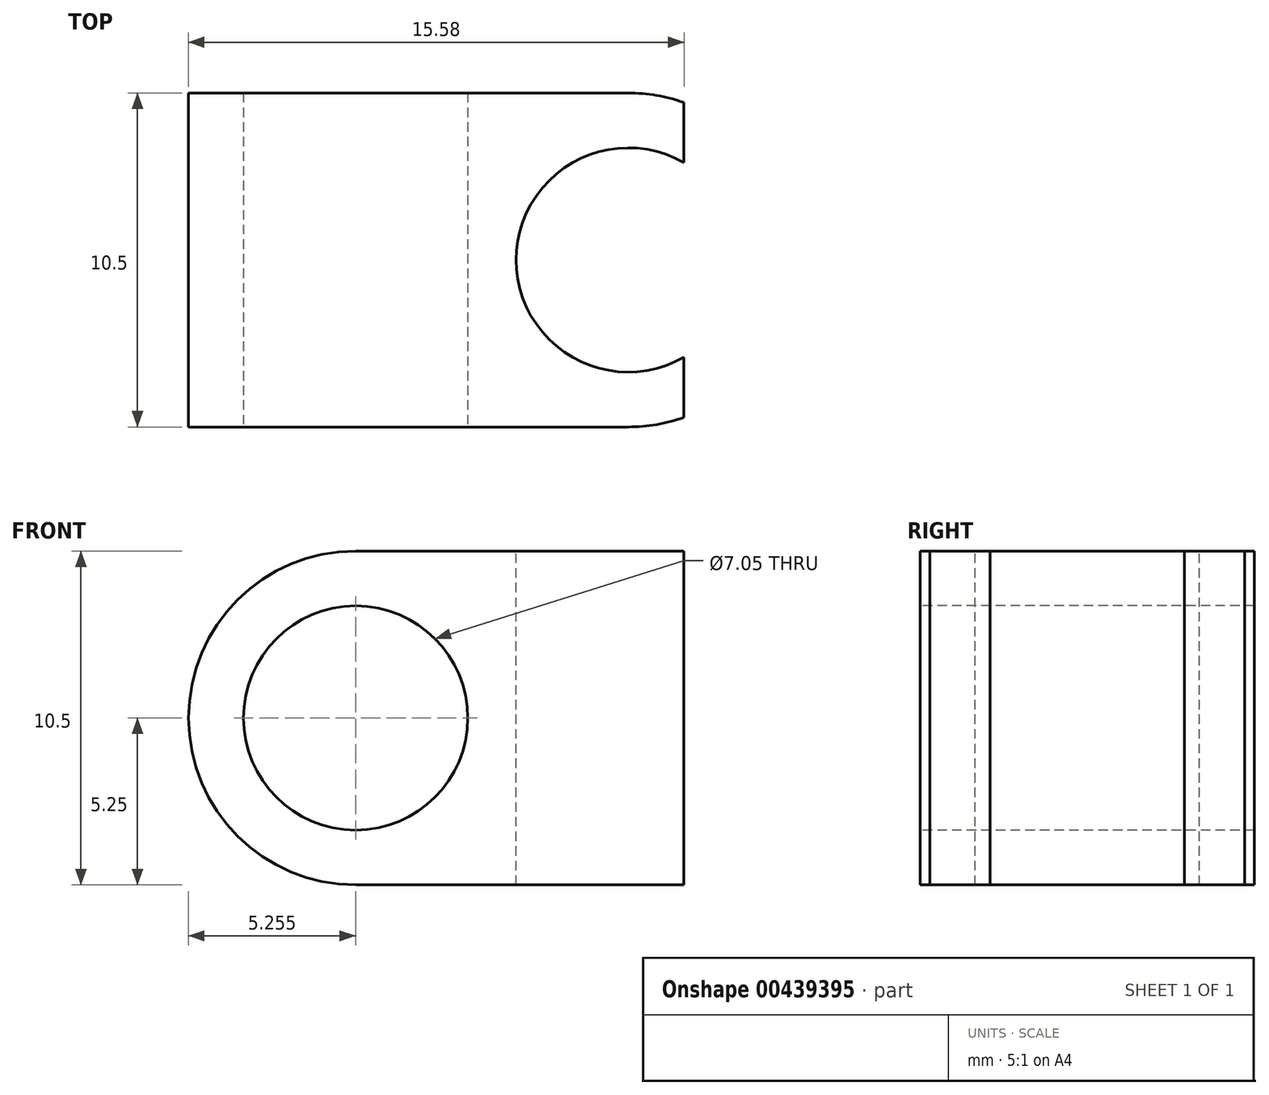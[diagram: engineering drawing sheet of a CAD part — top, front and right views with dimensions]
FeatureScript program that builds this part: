
annotation { "Feature Type Name" : "Feature", "Feature Type Description" : "" }
export const myFeature = defineFeature(function(context is Context, id is Id, definition is map)
    precondition{}
    {
        {
            var Q0;
            Q0=qCreatedBy(makeId("Front.planeOp"),FACE);
            var sketch = newSketch(context, id + "F0", { "sketchPlane" : qUnion([Q0])});
            skLineSegment(sketch, "E0.bottom", {"start": v(-9.53, 5.25) * mm, "end": v(9.54, 5.25) * mm});
            skLineSegment(sketch, "E0.top", {"start": v(-9.54, -5.25) * mm, "end": v(9.53, -5.25) * mm});
            skLineSegment(sketch, "E0.left", {"start": v(-9.53, 5.25) * mm, "end": v(-9.54, -5.25) * mm});
            skLineSegment(sketch, "E0.right", {"start": v(9.54, 5.25) * mm, "end": v(9.53, -5.25) * mm});
            skLineSegment(sketch, "E1", {"start": v(-9.53, 5.25) * mm, "end": v(9.53, -5.25) * mm, "construction": true});
            skLineSegment(sketch, "E2", {"start": v(9.54, 5.25) * mm, "end": v(-9.54, -5.25) * mm, "construction": true});
            skSolve(sketch);
        }
        {
            var Q0;
            Q0 = qSketchRegion(id + "F0", true);
            extrude(context, id + "F1", {"entities" : qUnion([Q0]), "oppositeDirection" : true, "depth" : 10.5 * mm});
        }
        {
            var Q0;
            Q0=makeQuery(id+"F1.opExtrude","CAP_FACE",FACE,{"disambiguationData":[OSD([sQuery(id+"F0.wireOp",EDGE,"E0.bottom"),sQuery(id+"F0.wireOp",EDGE,"E0.top"),sQuery(id+"F0.wireOp",EDGE,"E0.left"),sQuery(id+"F0.wireOp",EDGE,"E0.right")])],"isStart":true});
            var sketch = newSketch(context, id + "F2", { "sketchPlane" : qUnion([Q0])});
            skArc(sketch, "E3", {"start": v(-4.29, 5.25) * mm, "mid": v(-9.54, 0) * mm, "end": v(-4.29, -5.25) * mm});
            skCircle(sketch, "E4", {"center": v(-4.29, 0) * mm, "radius": 3.52 * mm});
            skLineSegment(sketch, "E5.0", {"start": v(-9.53, 5.25) * mm, "end": v(-4.29, 5.25) * mm});
            skLineSegment(sketch, "E6.0", {"start": v(-9.53, 5.25) * mm, "end": v(-9.54, -5.25) * mm});
            skLineSegment(sketch, "E7.0", {"start": v(-9.54, -5.25) * mm, "end": v(-4.29, -5.25) * mm});
            skPoint(sketch, "E8.orphan", {"position": v(9.54, 5.25) * mm});
            skPoint(sketch, "E9.orphan", {"position": v(9.53, -5.25) * mm});
            skSolve(sketch);
        }
        {
            var Q0;
            Q0 = qSketchRegion(id + "F2", true);
            extrude(context, id + "F3", {"entities" : qUnion([Q0]), "operationType" : NewBodyOperationType.REMOVE, "endBound" : BoundingType.UP_TO_NEXT, "oppositeDirection" : true, "depth" : 25 * mm});
        }
        {
            var Q0;
            Q0=makeQuery(id+"F1.opExtrude","SWEPT_FACE",FACE,{"disambiguationData":[OSD([sQuery(id+"F0.wireOp",EDGE,"E0.bottom")])]});
            var sketch = newSketch(context, id + "F4", { "sketchPlane" : qUnion([Q0])});
            skArc(sketch, "E10", {"start": v(4.29, 0) * mm, "mid": v(5.17, 0.08) * mm, "end": v(6.04, 0.3) * mm});
            skArc(sketch, "E11", {"start": v(6.04, 8.3) * mm, "mid": v(0.76, 5.25) * mm, "end": v(6.04, 2.2) * mm});
            skLineSegment(sketch, "E12", {"start": v(6.04, 10.2) * mm, "end": v(6.04, 8.3) * mm});
            skLineSegment(sketch, "E13.0", {"start": v(4.29, 10.5) * mm, "end": v(9.54, 10.5) * mm});
            skLineSegment(sketch, "E14.0", {"start": v(4.29, 0) * mm, "end": v(9.54, 0) * mm});
            skPoint(sketch, "E15.orphan", {"position": v(-4.29, 10.5) * mm});
            skPoint(sketch, "E16.orphan", {"position": v(-4.29, 0) * mm});
            skLineSegment(sketch, "E17.0.0", {"start": v(9.54, 10.5) * mm, "end": v(4.29, 10.5) * mm});
            skLineSegment(sketch, "E17.0.3", {"start": v(9.54, 0) * mm, "end": v(9.54, 10.5) * mm});
            skLineSegment(sketch, "E18.trimOffspring", {"start": v(6.04, 2.2) * mm, "end": v(6.04, 0.3) * mm});
            skArc(sketch, "E19.trimOffspring", {"start": v(6.04, 10.2) * mm, "mid": v(5.17, 10.42) * mm, "end": v(4.29, 10.5) * mm});
            skPoint(sketch, "E20.orphan", {"position": v(6.04, 0) * mm});
            skSolve(sketch);
        }
        {
            var Q0;
            Q0 = qSketchRegion(id + "F4", true);
            extrude(context, id + "F5", {"entities" : qUnion([Q0]), "operationType" : NewBodyOperationType.REMOVE, "endBound" : BoundingType.UP_TO_NEXT, "oppositeDirection" : true, "depth" : 25 * mm});
        }
    });
